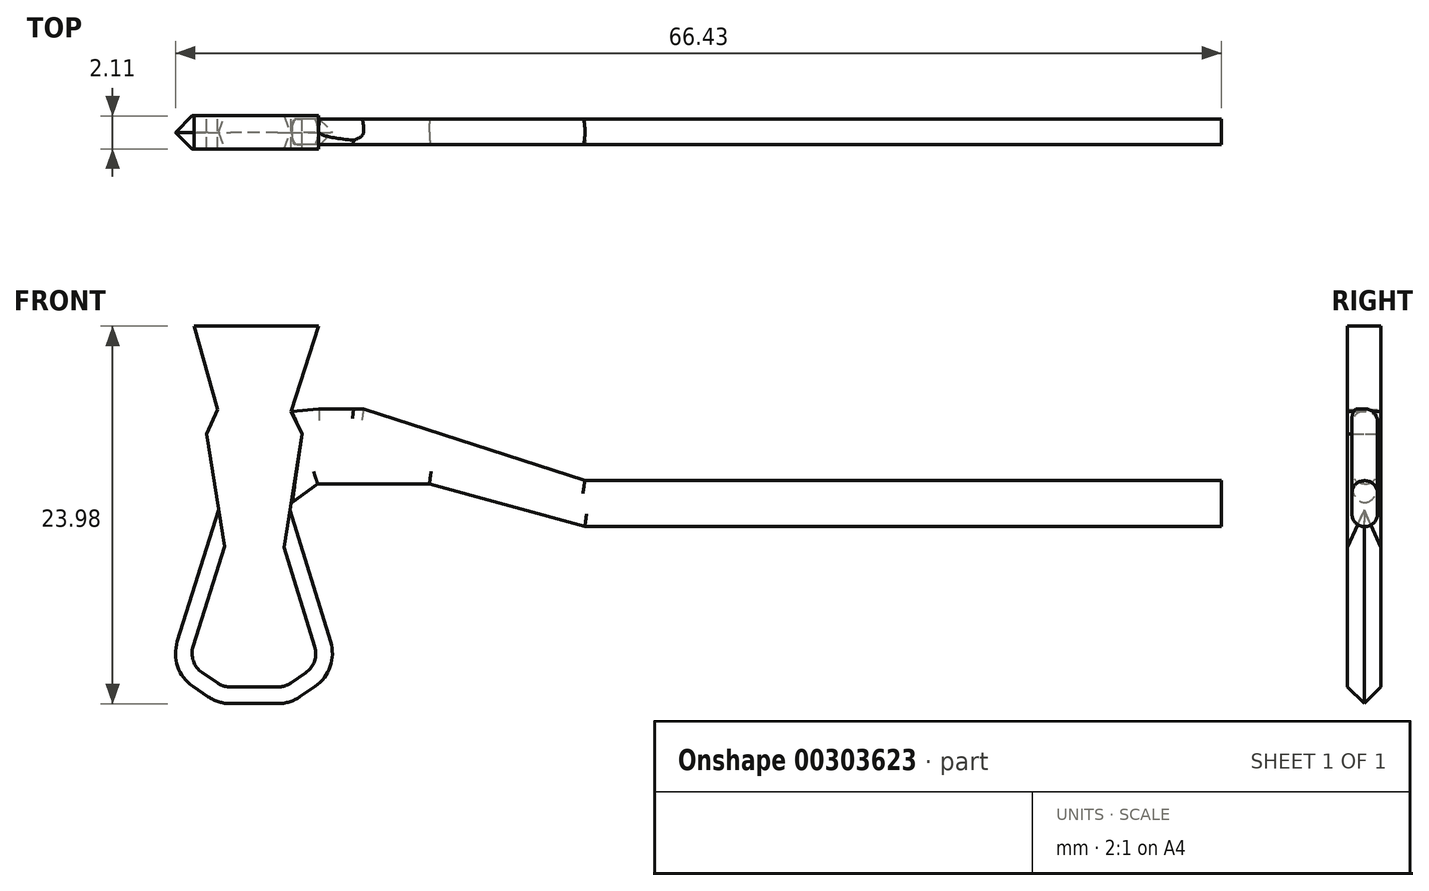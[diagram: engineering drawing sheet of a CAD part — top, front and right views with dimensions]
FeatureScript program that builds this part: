
annotation { "Feature Type Name" : "Feature", "Feature Type Description" : "" }
export const myFeature = defineFeature(function(context is Context, id is Id, definition is map)
    precondition{}
    {
        {
            var Q0;
            Q0=qCreatedBy(makeId("Front.planeOp"),FACE);
            var sketch = newSketch(context, id + "F0", { "sketchPlane" : qUnion([Q0])});
            skLineSegment(sketch, "E0", {"start": v(22.13, 19.87) * mm, "end": v(-18.3, 19.87) * mm});
            skLineSegment(sketch, "E1", {"start": v(-18.3, 19.87) * mm, "end": v(-32.35, 24.44) * mm});
            skLineSegment(sketch, "E2", {"start": v(-32.35, 24.44) * mm, "end": v(-35.2, 24.44) * mm});
            skLineSegment(sketch, "E3", {"start": v(22.13, 19.87) * mm, "end": v(22.13, 16.97) * mm});
            skLineSegment(sketch, "E4", {"start": v(22.13, 16.97) * mm, "end": v(-18.3, 16.97) * mm});
            skLineSegment(sketch, "E5", {"start": v(-18.3, 16.97) * mm, "end": v(-28.18, 19.65) * mm});
            skLineSegment(sketch, "E6", {"start": v(-28.18, 19.65) * mm, "end": v(-35.27, 19.65) * mm});
            skLineSegment(sketch, "E7", {"start": v(-36.96, 24.28) * mm, "end": v(-35.2, 29.69) * mm});
            skLineSegment(sketch, "E8", {"start": v(-35.2, 29.69) * mm, "end": v(-43.13, 29.69) * mm});
            skLineSegment(sketch, "E9", {"start": v(-36.96, 24.28) * mm, "end": v(-36.27, 22.84) * mm});
            skLineSegment(sketch, "E10", {"start": v(-36.27, 22.84) * mm, "end": v(-36.96, 18.48) * mm});
            skLineSegment(sketch, "E11", {"start": v(-43.13, 29.69) * mm, "end": v(-41.64, 24.4) * mm});
            skLineSegment(sketch, "E12", {"start": v(-41.64, 24.4) * mm, "end": v(-42.34, 22.84) * mm});
            skLineSegment(sketch, "E13", {"start": v(-42.34, 22.84) * mm, "end": v(-41.64, 18.48) * mm});
            skLineSegment(sketch, "E14", {"start": v(-41.64, 18.48) * mm, "end": v(-45, 7.78) * mm});
            skLineSegment(sketch, "E15", {"start": v(-45, 7.78) * mm, "end": v(-41.64, 5.5) * mm});
            skLineSegment(sketch, "E16", {"start": v(-41.64, 5.5) * mm, "end": v(-36.96, 5.5) * mm});
            skLineSegment(sketch, "E17", {"start": v(-36.96, 5.5) * mm, "end": v(-33.65, 7.78) * mm});
            skLineSegment(sketch, "E18", {"start": v(-33.65, 7.78) * mm, "end": v(-36.96, 18.48) * mm});
            skLineSegment(sketch, "E19", {"start": v(-35.27, 19.65) * mm, "end": v(-36.88, 18.48) * mm});
            skLineSegment(sketch, "E20", {"start": v(-35.2, 24.44) * mm, "end": v(-36.92, 24.28) * mm});
            skLineSegment(sketch, "E21", {"start": v(-36.92, 24.28) * mm, "end": v(-36.27, 22.84) * mm});
            skLineSegment(sketch, "E22", {"start": v(-36.27, 22.84) * mm, "end": v(-36.88, 18.48) * mm});
            skSolve(sketch);
        }
        {
            var Q0;
            Q0=makeQuery(id+"F0.imprint","IMPRINT",FACE,{"disambiguationData":[TD([[makeQuery(id+"F0.imprint","IMPRINT",EDGE,{"derivedFrom":sQuery(id+"F0.wireOp",EDGE,"E7")}),1.0]])]});
            extrude(context, id + "F1", {"entities" : qUnion([Q0]), "depth" : 1.9 * mm, "hasSecondDirection" : true, "secondDirectionOppositeDirection" : true, "secondDirectionDepth" : 0.2 * mm});
        }
        {
            var Q0;
            Q0=makeQuery(id+"F1.opExtrude","SWEPT_EDGE",EDGE,{"disambiguationData":[OSD([sQuery(id+"F0.wireOp",EDGE,"E16"),sQuery(id+"F0.wireOp",EDGE,"E17")])]});
            var Q1;
            Q1=makeQuery(id+"F1.opExtrude","SWEPT_EDGE",EDGE,{"disambiguationData":[OSD([sQuery(id+"F0.wireOp",EDGE,"E17"),sQuery(id+"F0.wireOp",EDGE,"E18")])]});
            var Q2;
            Q2=makeQuery(id+"F1.opExtrude","SWEPT_EDGE",EDGE,{"disambiguationData":[OSD([sQuery(id+"F0.wireOp",EDGE,"E14"),sQuery(id+"F0.wireOp",EDGE,"E15")])]});
            var Q3;
            Q3=makeQuery(id+"F1.opExtrude","SWEPT_EDGE",EDGE,{"disambiguationData":[OSD([sQuery(id+"F0.wireOp",EDGE,"E15"),sQuery(id+"F0.wireOp",EDGE,"E16")])]});
            fillet(context, id + "F2", {"entities" : qUnion([Q0, Q1, Q2, Q3]), "radius" : 2.75 * mm, "tangentPropagation" : true, "allowEdgeOverflow" : false});
        }
        {
            var Q0;
            Q0=makeQuery(id+"F2.opFillet","BLEND_FACE",FACE,{"disambiguationData":[OSD([sQuery(id+"F0.wireOp",EDGE,"E17"),sQuery(id+"F0.wireOp",EDGE,"E18")])]});
            chamfer(context, id + "F3", {"entities" : qUnion([Q0]), "width" : 1.27 * mm, "tangentPropagation" : true});
        }
        {
            var Q0;
            Q0=makeQuery(id+"F0.imprint","IMPRINT",FACE,{"disambiguationData":[TD([[makeQuery(id+"F0.imprint","IMPRINT",EDGE,{"derivedFrom":sQuery(id+"F0.wireOp",EDGE,"E0")}),1.0]])]});
            extrude(context, id + "F4", {"entities" : qUnion([Q0]), "depth" : 1.63 * mm});
        }
        {
            var Q0;
            Q0=makeQuery(id+"F4.opExtrude","CAP_EDGE",EDGE,{"disambiguationData":[OSD([sQuery(id+"F0.wireOp",EDGE,"E4")])],"isStart":false});
            var Q1;
            Q1=makeQuery(id+"F4.opExtrude","CAP_EDGE",EDGE,{"disambiguationData":[OSD([sQuery(id+"F0.wireOp",EDGE,"E0")])],"isStart":false});
            var Q2;
            Q2=makeQuery(id+"F4.opExtrude","CAP_EDGE",EDGE,{"disambiguationData":[OSD([sQuery(id+"F0.wireOp",EDGE,"E4")])],"isStart":true});
            var Q3;
            Q3=makeQuery(id+"F4.opExtrude","CAP_EDGE",EDGE,{"disambiguationData":[OSD([sQuery(id+"F0.wireOp",EDGE,"E0")])],"isStart":true});
            var Q4;
            Q4=makeQuery(id+"F4.opExtrude","CAP_EDGE",EDGE,{"disambiguationData":[OSD([sQuery(id+"F0.wireOp",EDGE,"E5")])],"isStart":false});
            var Q5;
            Q5=makeQuery(id+"F4.opExtrude","CAP_EDGE",EDGE,{"disambiguationData":[OSD([sQuery(id+"F0.wireOp",EDGE,"E5")])],"isStart":true});
            var Q6;
            Q6=makeQuery(id+"F4.opExtrude","CAP_EDGE",EDGE,{"disambiguationData":[OSD([sQuery(id+"F0.wireOp",EDGE,"E1")])],"isStart":false});
            var Q7;
            Q7=makeQuery(id+"F4.opExtrude","CAP_EDGE",EDGE,{"disambiguationData":[OSD([sQuery(id+"F0.wireOp",EDGE,"E6")])],"isStart":false});
            var Q8;
            Q8=makeQuery(id+"F4.opExtrude","CAP_EDGE",EDGE,{"disambiguationData":[OSD([sQuery(id+"F0.wireOp",EDGE,"E6")])],"isStart":true});
            var Q9;
            Q9=makeQuery(id+"F4.opExtrude","CAP_EDGE",EDGE,{"disambiguationData":[OSD([sQuery(id+"F0.wireOp",EDGE,"E20")])],"isStart":false});
            var Q10;
            Q10=makeQuery(id+"F4.opExtrude","CAP_EDGE",EDGE,{"disambiguationData":[OSD([sQuery(id+"F0.wireOp",EDGE,"E19")])],"isStart":false});
            var Q11;
            Q11=makeQuery(id+"F4.opExtrude","CAP_EDGE",EDGE,{"disambiguationData":[OSD([sQuery(id+"F0.wireOp",EDGE,"E19")])],"isStart":true});
            var Q12;
            Q12=makeQuery(id+"F4.opExtrude","CAP_EDGE",EDGE,{"disambiguationData":[OSD([sQuery(id+"F0.wireOp",EDGE,"E20")])],"isStart":true});
            var Q13;
            Q13=makeQuery(id+"F4.opExtrude","CAP_EDGE",EDGE,{"disambiguationData":[OSD([sQuery(id+"F0.wireOp",EDGE,"E2")])],"isStart":true});
            var Q14;
            Q14=makeQuery(id+"F4.opExtrude","CAP_EDGE",EDGE,{"disambiguationData":[OSD([sQuery(id+"F0.wireOp",EDGE,"E1")])],"isStart":true});
            fillet(context, id + "F5", {"entities" : qUnion([Q0, Q1, Q2, Q3, Q4, Q5, Q6, Q7, Q8, Q9, Q10, Q11, Q12, Q13, Q14]), "radius" : 0.8 * mm, "tangentPropagation" : true, "allowEdgeOverflow" : false});
        }
    });
